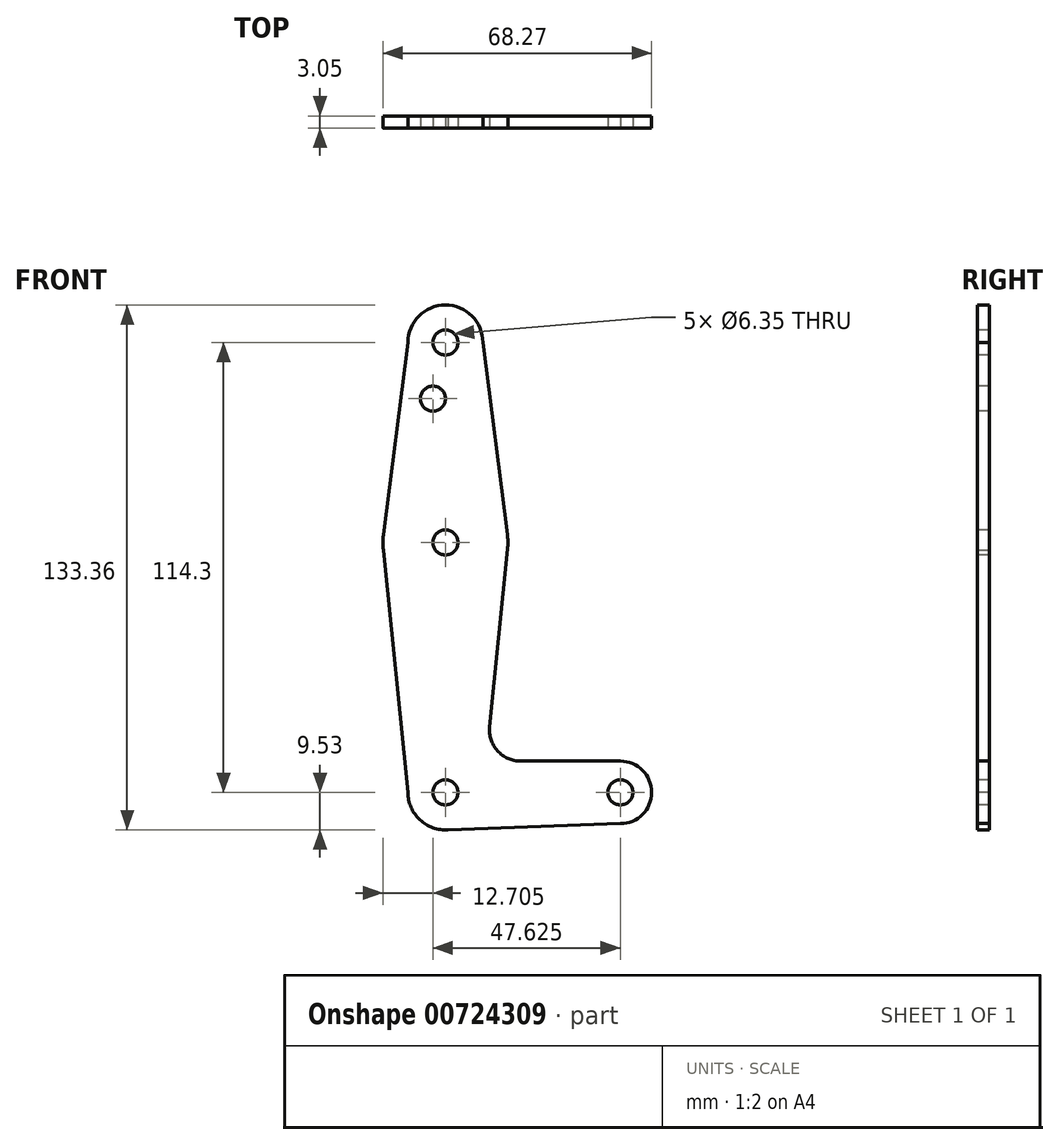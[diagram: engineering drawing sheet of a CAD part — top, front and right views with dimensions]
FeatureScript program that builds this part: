
annotation { "Feature Type Name" : "Feature", "Feature Type Description" : "" }
export const myFeature = defineFeature(function(context is Context, id is Id, definition is map)
    precondition{}
    {
        {
            var Q0;
            Q0=qCreatedBy(makeId("Front.planeOp"),FACE);
            var sketch = newSketch(context, id + "F0", { "sketchPlane" : qUnion([Q0])});
            skLineSegment(sketch, "E0", {"start": v(0, 0) * mm, "end": v(44.45, 0) * mm, "construction": true});
            skCircle(sketch, "E1", {"center": v(44.45, 0) * mm, "radius": 7.94 * mm});
            skCircle(sketch, "E2", {"center": v(0, 0) * mm, "radius": 9.53 * mm});
            skCircle(sketch, "E3", {"center": v(0, 114.3) * mm, "radius": 9.53 * mm});
            skLineSegment(sketch, "E4", {"start": v(0, 0) * mm, "end": v(0, 114.3) * mm, "construction": true});
            skCircle(sketch, "E5", {"center": v(0, 63.5) * mm, "radius": 15.88 * mm});
            skLineSegment(sketch, "E6", {"start": v(-9.53, 114.3) * mm, "end": v(-15.75, 65.5) * mm});
            skLineSegment(sketch, "E7", {"start": v(9.52, 114.3) * mm, "end": v(15.75, 65.5) * mm});
            skLineSegment(sketch, "E8", {"start": v(-15.75, 61.5) * mm, "end": v(-9.52, 0) * mm});
            skLineSegment(sketch, "E9", {"start": v(15.8, 61.9) * mm, "end": v(11.22, 16.69) * mm});
            skLineSegment(sketch, "E10", {"start": v(19.12, 7.94) * mm, "end": v(44.45, 7.94) * mm});
            skLineSegment(sketch, "E11", {"start": v(0, -9.53) * mm, "end": v(44.45, -7.94) * mm});
            skCircle(sketch, "E12", {"center": v(-3.18, 100.03) * mm, "radius": 3.18 * mm});
            skCircle(sketch, "E13", {"center": v(0, 63.5) * mm, "radius": 3.18 * mm});
            skCircle(sketch, "E14", {"center": v(0, 114.3) * mm, "radius": 3.18 * mm});
            skCircle(sketch, "E15", {"center": v(0, 0) * mm, "radius": 3.18 * mm});
            skCircle(sketch, "E16", {"center": v(44.45, 0) * mm, "radius": 3.18 * mm});
            skArc(sketch, "E17.filletArc", {"start": v(11.22, 16.69) * mm, "mid": v(13.23, 10.56) * mm, "end": v(19.12, 7.94) * mm});
            skSolve(sketch);
        }
        {
            var Q0;
            Q0 = qSketchRegion(id + "F0", true);
            extrude(context, id + "F1", {"entities" : qUnion([Q0]), "oppositeDirection" : true, "depth" : 3.05 * mm, "offsetDistance" : 25.4 * mm});
        }
    });
